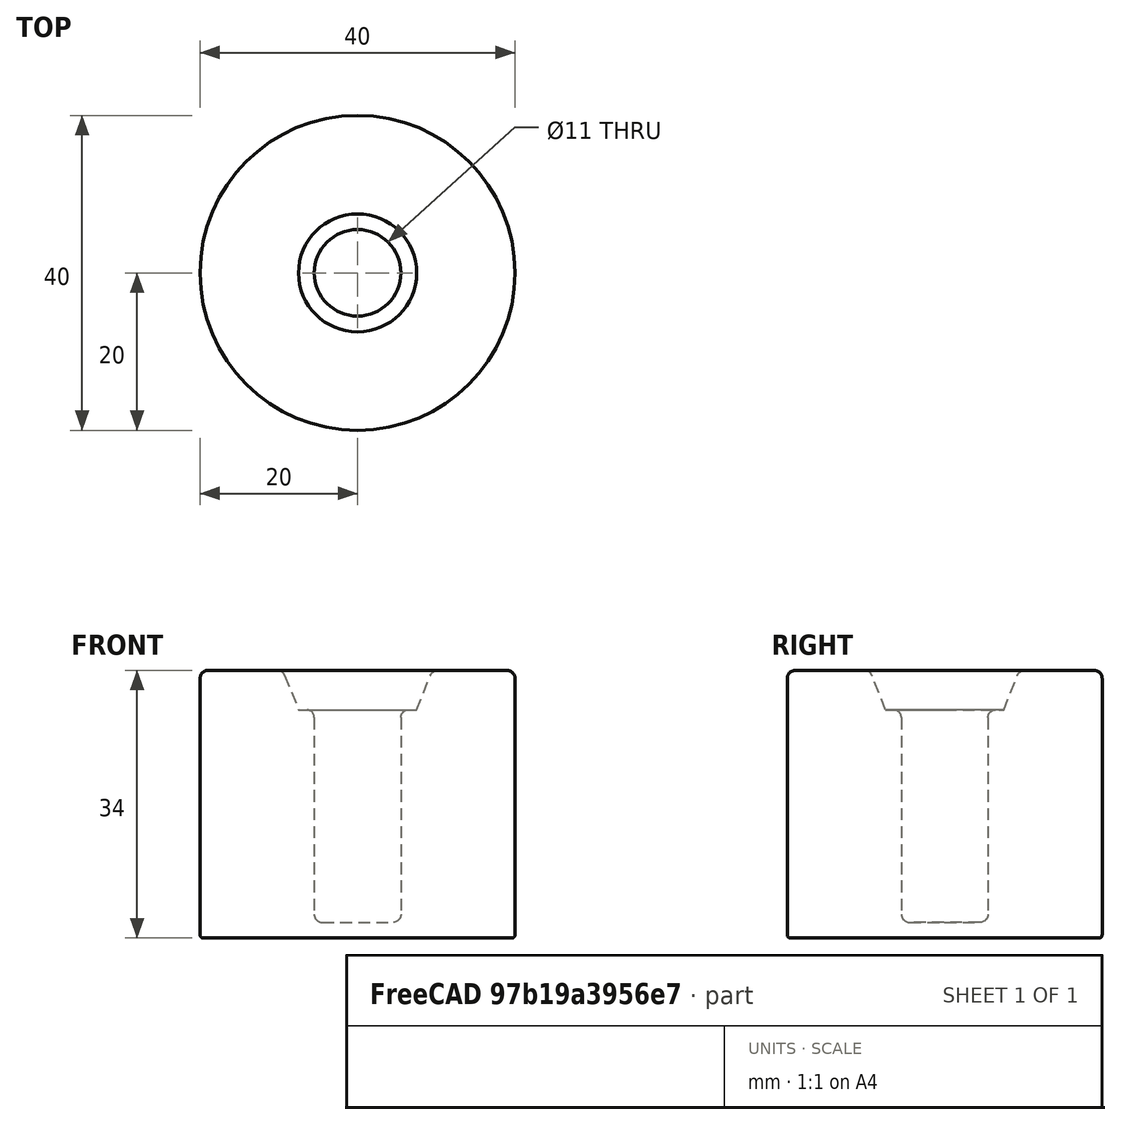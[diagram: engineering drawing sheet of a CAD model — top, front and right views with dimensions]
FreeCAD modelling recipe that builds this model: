
FCSTD DOCUMENT  (FreeCAD 0.19R)
Label: es-126_stand
License: All rights reserved
LicenseURL: http://en.wikipedia.org/wiki/All_rights_reserved
objects: PartDesign::Fillet×2, PartDesign::AdditiveCylinder×1, PartDesign::Plane×1, PartDesign::SubtractiveCylinder×1, PartDesign::SubtractiveCone×1, PartDesign::Body×1
note: 12 computed .brp shape members not serialized (recipe doc carries the construction recipe); baked Part::Feature solids carry a one-line shape summary decoded from their .brp

FEATURE [PartDesign::AdditiveCylinder] Cylinder
  Angle = 360
  AttacherType = Attacher::AttachEngine3D
  Height = 34
  Radius = 20
  Refine = true
FEATURE [PartDesign::Plane] DatumPlane
  Length = 60
  MapMode = 5
  Placement = pos=(0,0,34) rot=(0,0,1;0rad)
  ResizeMode = 0
  Support = -> [Cylinder]
  Width = 60
FEATURE [PartDesign::SubtractiveCylinder] Cylinder001
  Angle = 360
  AttacherType = Attacher::AttachEngine3D
  BaseFeature = -> Cylinder
  Height = 32
  MapMode = 5
  Placement = pos=(0,0,34) rot=(0,1,0;3.14159rad)
  Radius = 5.5
  Refine = true
  Support = -> [Cylinder]
FEATURE [PartDesign::SubtractiveCone] Cone
  Angle = 360
  AttacherType = Attacher::AttachEngine3D
  BaseFeature = -> Cylinder001
  Height = 5
  MapMode = 5
  Placement = pos=(0,0,34) rot=(0,1,0;3.14159rad)
  Radius1 = 9.5
  Radius2 = 7.5
  Refine = true
  Support = -> [DatumPlane]
FEATURE [PartDesign::Fillet] Fillet
  Base = -> Cone [Edge1,Edge4,Edge7,Edge9]
  BaseFeature = -> Cone
  Placement = pos=(0,0,34) rot=(0,1,0;3.14159rad)
  Radius = 1
  Refine = true
  SupportTransform = false
FEATURE [PartDesign::Fillet] Fillet001
  Base = -> Fillet [Edge3]
  BaseFeature = -> Fillet
  Placement = pos=(0,0,34) rot=(0,1,0;3.14159rad)
  Radius = 0.4
  Refine = true
  SupportTransform = false
FEATURE [PartDesign::Body] Body
  Group = -> [Cylinder,DatumPlane,Cylinder001,Cone,Fillet,Fillet001]
  Origin = -> Origin
  Tip = -> Fillet001
